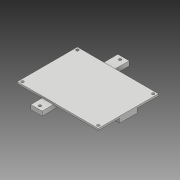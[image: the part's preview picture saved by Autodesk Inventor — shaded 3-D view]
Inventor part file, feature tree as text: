
AUTODESK INVENTOR PART (.ipt)
format: ipt  version: 2018 (Build 220112000, 112)  size: 165,376 bytes
history: native  units: mm
features: extrude x4, sketch x4, other x1
ambient origin geometry x8: Origin, YZ Plane, XZ Plane, XY Plane, X Axis, Y Axis, Z Axis, Center Point
bodies: Body1 (feature_tree)
feature tree (9):
  other  "Sólido1"
  extrude  "Extrusión1"  Depth=63.0mm
  extrude  "Extrusión2"  Depth=3.0mm
  extrude  "Extrusión3"  Depth=3.0mm
  extrude  "Extrusión4"  Depth=3.0mm
  sketch  "Boceto1"  dims[d0=87.0mm d1=63.0mm]
  sketch  "Boceto2"  dims[d2=3.0mm d3=3.0mm]
  sketch  "Boceto3"  dims[d4=3.0mm d5=3.0mm]
  sketch  "Boceto4"  dims[d8=3.0mm d9=3.0mm d10=3.0mm d11=2.0mm d12=0.0mm d13=12.0mm d14=17.0mm d15=32.0mm d16=3.0mm d17=3.0mm d18=6.5mm d19=4.0mm d20=13.0mm d21=4.0mm d22=10.0mm d23=10.0mm d24=20.0mm d25=5.0mm d26=0.0mm d27=6.0mm d28=6.0mm d29=2.0mm d30=0.0mm d31=5.0mm d32=2.0mm d33=41.5mm d34=5.0mm d35=18.5mm d36=2.0mm d37=0.0mm]
